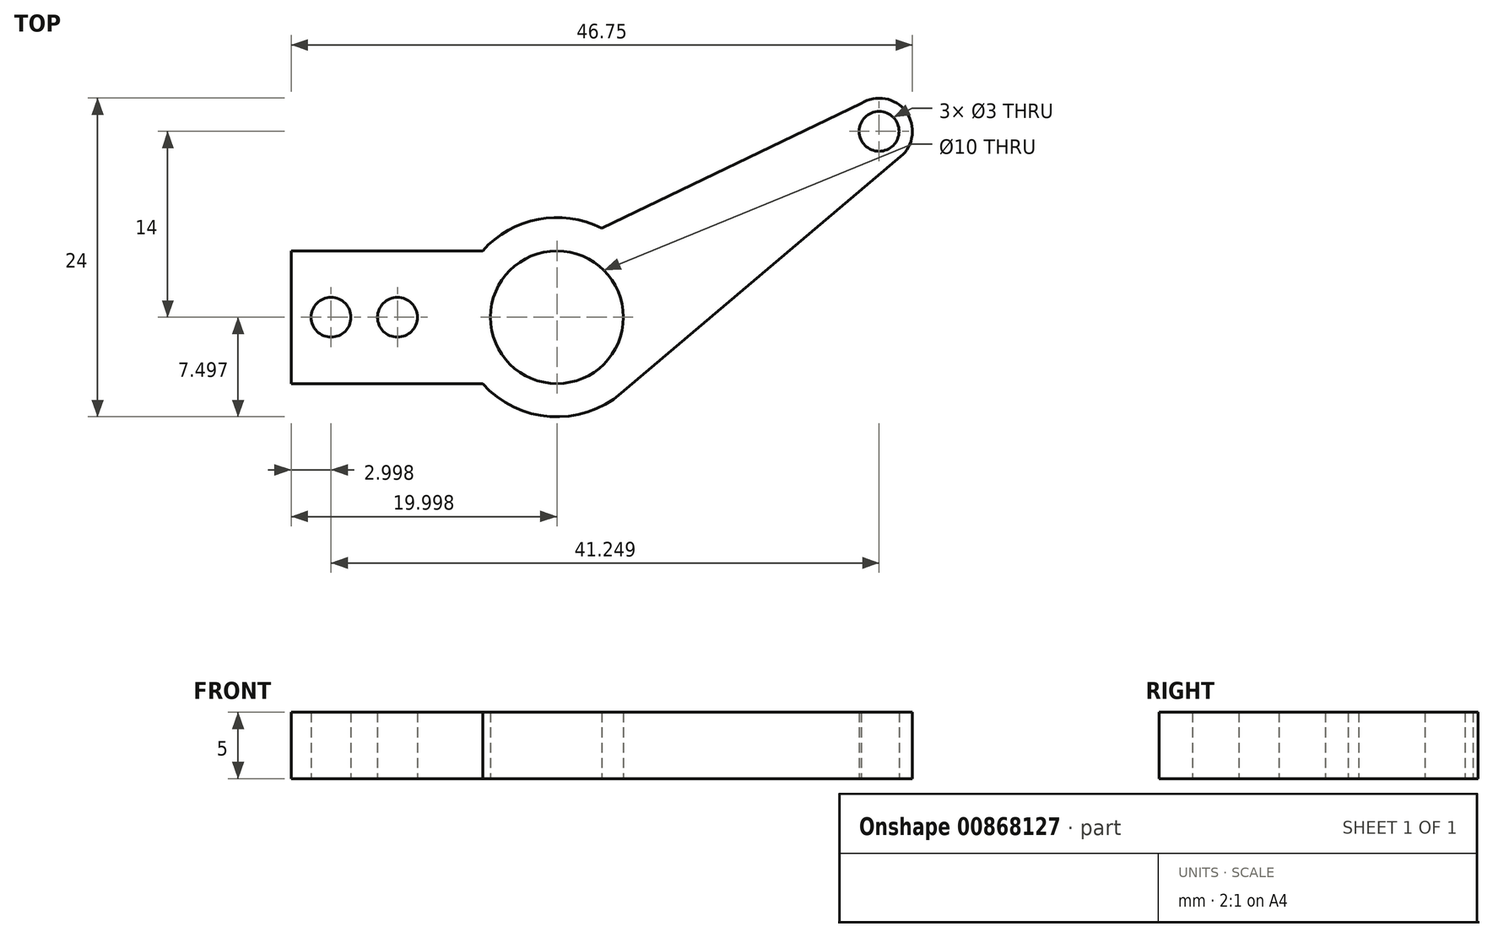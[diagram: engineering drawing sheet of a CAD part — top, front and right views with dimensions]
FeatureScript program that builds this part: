
annotation { "Feature Type Name" : "Feature", "Feature Type Description" : "" }
export const myFeature = defineFeature(function(context is Context, id is Id, definition is map)
    precondition{}
    {
        {
            var Q0;
            Q0=qCreatedBy(makeId("Top.planeOp"),FACE);
            var sketch = newSketch(context, id + "F0", { "sketchPlane" : qUnion([Q0])});
            skLineSegment(sketch, "E0.bottom", {"start": v(-28.01, 6.7) * mm, "end": v(-13.6, 6.7) * mm});
            skLineSegment(sketch, "E0.top", {"start": v(-28.01, -3.3) * mm, "end": v(-13.6, -3.3) * mm});
            skLineSegment(sketch, "E0.left", {"start": v(-28.01, 6.7) * mm, "end": v(-28.01, -3.3) * mm});
            skPoint(sketch, "E1", {"position": v(-8.01, 1.7) * mm});
            skArc(sketch, "E2", {"start": v(-4.65, 8.4) * mm, "mid": v(-9.41, 9.07) * mm, "end": v(-13.6, 6.7) * mm});
            skCircle(sketch, "E3", {"center": v(-8.01, 1.7) * mm, "radius": 5 * mm});
            skPoint(sketch, "E4", {"position": v(-25.01, 1.7) * mm});
            skPoint(sketch, "E5", {"position": v(-20.01, 1.7) * mm});
            skCircle(sketch, "E6", {"center": v(-25.01, 1.7) * mm, "radius": 1.5 * mm});
            skCircle(sketch, "E7", {"center": v(-20.01, 1.7) * mm, "radius": 1.5 * mm});
            skCircle(sketch, "E8", {"center": v(16.24, 15.7) * mm, "radius": 1.5 * mm});
            skCircle(sketch, "E9", {"center": v(16.24, 15.7) * mm, "radius": 2.5 * mm});
            skPoint(sketch, "E10.orphan", {"position": v(-8.01, -3.3) * mm});
            skPoint(sketch, "E11.start.orphan", {"position": v(-8.01, 6.7) * mm});
            skArc(sketch, "E12.trimOffspring", {"start": v(-13.6, -3.3) * mm, "mid": v(-8.53, -5.79) * mm, "end": v(-3.16, -4.02) * mm});
            skPoint(sketch, "E13.start.orphan", {"position": v(-28.01, 1.7) * mm});
            skLineSegment(sketch, "E14", {"start": v(14.89, 17.8) * mm, "end": v(-4.65, 8.4) * mm});
            skLineSegment(sketch, "E15", {"start": v(17.85, 13.79) * mm, "end": v(-3.16, -4.02) * mm});
            skSolve(sketch);
        }
        {
            var Q0;
            Q0 = qSketchRegion(id + "F0", true);
            extrude(context, id + "F1", {"entities" : qUnion([Q0]), "depth" : 5 * mm, "offsetDistance" : 25 * mm});
        }
    });
